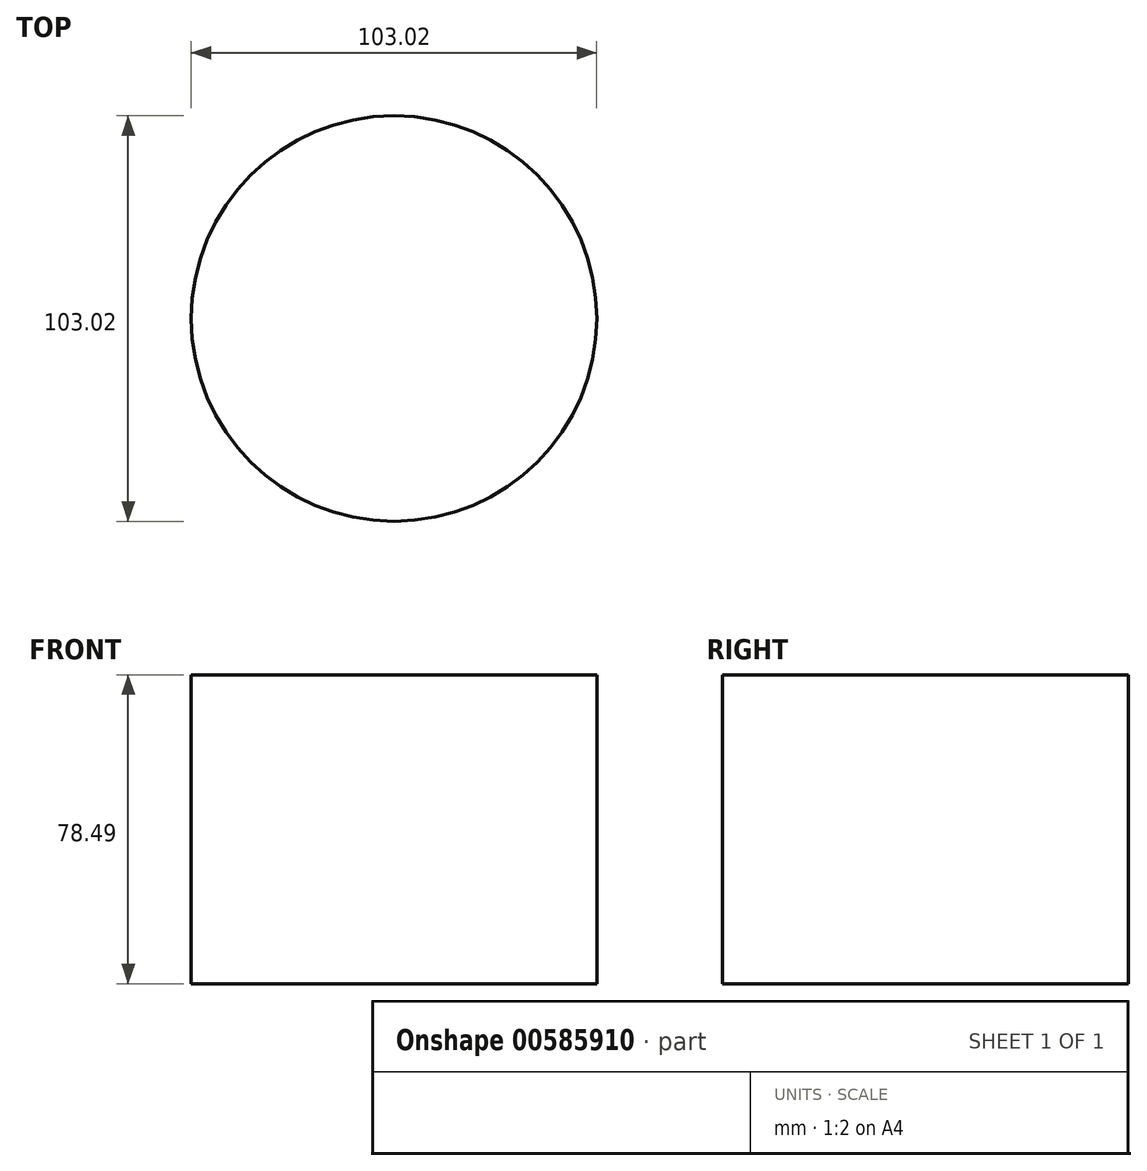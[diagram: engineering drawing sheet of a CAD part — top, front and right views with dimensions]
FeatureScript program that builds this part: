
annotation { "Feature Type Name" : "Feature", "Feature Type Description" : "" }
export const myFeature = defineFeature(function(context is Context, id is Id, definition is map)
    precondition{}
    {
        {
            var Q0;
            Q0=qCreatedBy(makeId("Top.planeOp"),FACE);
            var sketch = newSketch(context, id + "F0", { "sketchPlane" : qUnion([Q0])});
            skCircle(sketch, "E0", {"center": v(-109.56, -18.07) * mm, "radius": 51.51 * mm});
            skSolve(sketch);
        }
        {
            var Q0;
            Q0 = qSketchRegion(id + "F0", true);
            extrude(context, id + "F1", {"entities" : qUnion([Q0]), "depth" : 78.49 * mm, "offsetDistance" : 25.4 * mm});
        }
    });
